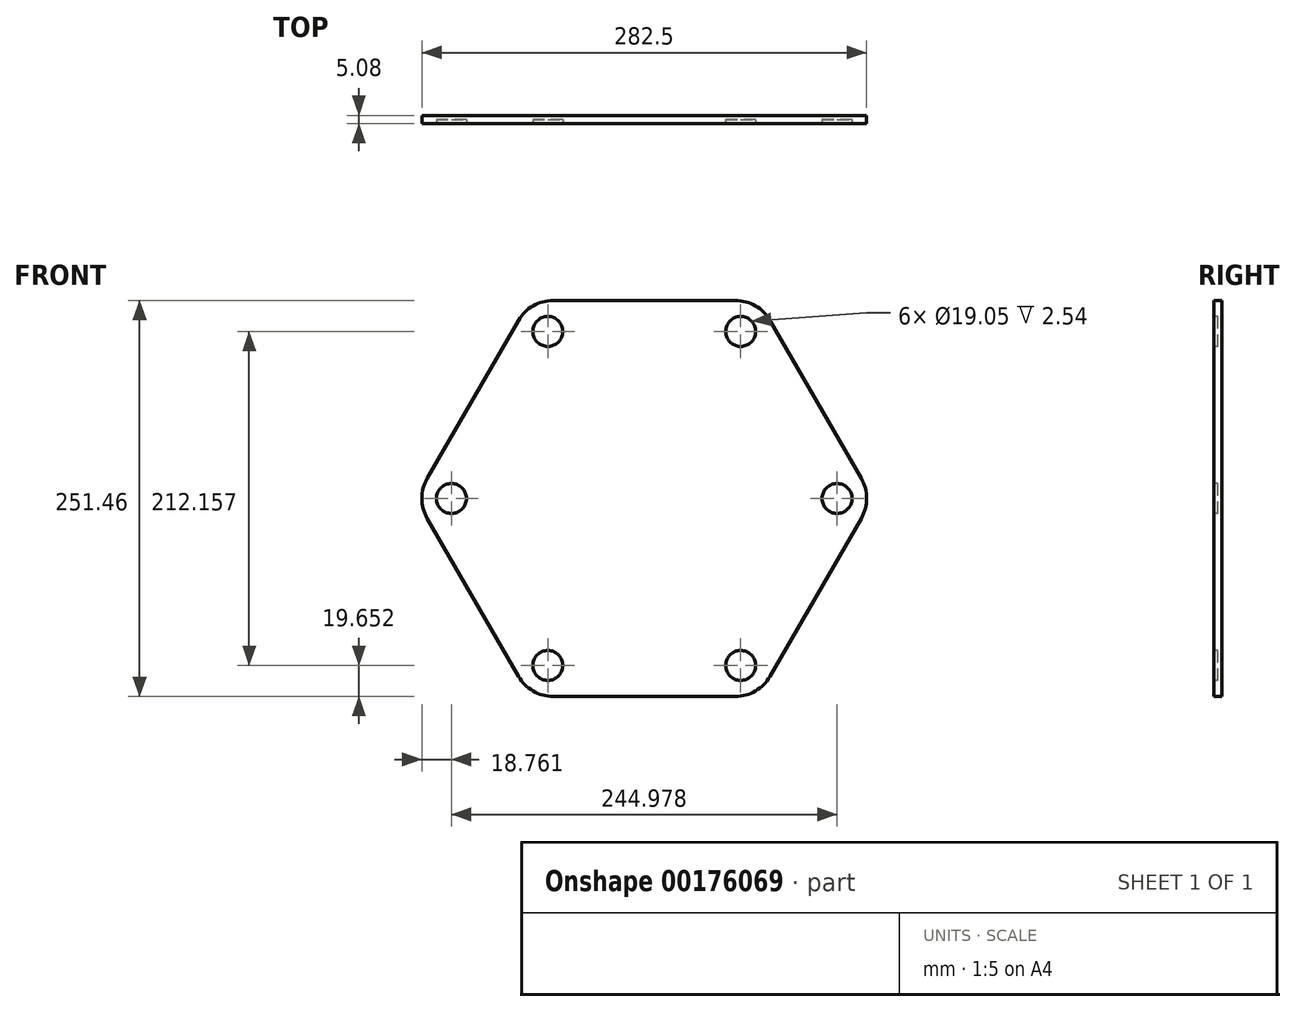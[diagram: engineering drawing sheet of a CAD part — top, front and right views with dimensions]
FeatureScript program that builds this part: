
annotation { "Feature Type Name" : "Feature", "Feature Type Description" : "" }
export const myFeature = defineFeature(function(context is Context, id is Id, definition is map)
    precondition{}
    {
        {
            var Q0;
            Q0=qCreatedBy(makeId("Front.planeOp"),FACE);
            var sketch = newSketch(context, id + "F0", { "sketchPlane" : qUnion([Q0])});
            skCircle(sketch, "E0.cCircle", {"center": v(0, 0) * mm, "radius": 125.73 * mm, "construction": true});
            skLineSegment(sketch, "E0.0", {"start": v(-57.93, 125.73) * mm, "end": v(57.93, 125.73) * mm});
            skLineSegment(sketch, "E0.1", {"start": v(79.92, 113.03) * mm, "end": v(137.85, 12.7) * mm});
            skLineSegment(sketch, "E0.2", {"start": v(137.85, -12.7) * mm, "end": v(79.92, -113.03) * mm});
            skLineSegment(sketch, "E0.3", {"start": v(57.93, -125.73) * mm, "end": v(-57.93, -125.73) * mm});
            skLineSegment(sketch, "E0.4", {"start": v(-79.92, -113.03) * mm, "end": v(-137.85, -12.7) * mm});
            skLineSegment(sketch, "E0.5", {"start": v(-137.85, 12.7) * mm, "end": v(-79.92, 113.03) * mm});
            skPoint(sketch, "E0.0.midPoint", {"position": v(0, 125.73) * mm});
            skPoint(sketch, "E1.visualSharp", {"position": v(-72.6, 125.73) * mm});
            skArc(sketch, "E1.filletArc", {"start": v(-57.93, 125.73) * mm, "mid": v(-70.63, 122.33) * mm, "end": v(-79.92, 113.03) * mm});
            skPoint(sketch, "E2.visualSharp", {"position": v(72.6, 125.73) * mm});
            skArc(sketch, "E2.filletArc", {"start": v(79.92, 113.03) * mm, "mid": v(70.63, 122.33) * mm, "end": v(57.93, 125.73) * mm});
            skPoint(sketch, "E3.visualSharp", {"position": v(145.18, 0) * mm});
            skArc(sketch, "E3.filletArc", {"start": v(137.85, -12.7) * mm, "mid": v(141.25, 0) * mm, "end": v(137.85, 12.7) * mm});
            skPoint(sketch, "E4.visualSharp", {"position": v(72.6, -125.73) * mm});
            skArc(sketch, "E4.filletArc", {"start": v(57.93, -125.73) * mm, "mid": v(70.63, -122.33) * mm, "end": v(79.92, -113.03) * mm});
            skPoint(sketch, "E5.visualSharp", {"position": v(-72.6, -125.73) * mm});
            skArc(sketch, "E5.filletArc", {"start": v(-79.92, -113.03) * mm, "mid": v(-70.63, -122.33) * mm, "end": v(-57.93, -125.73) * mm});
            skPoint(sketch, "E6.visualSharp", {"position": v(-145.18, 0) * mm});
            skArc(sketch, "E6.filletArc", {"start": v(-137.85, 12.7) * mm, "mid": v(-141.25, 0) * mm, "end": v(-137.85, -12.7) * mm});
            skSolve(sketch);
        }
        {
            var Q0;
            Q0=qSketchRegion(id+"F0",true);
            extrude(context, id + "F1", {"entities" : qUnion([Q0]), "depth" : 5.08 * mm});
        }
        {
            var Q0;
            Q0=makeQuery(id+"F1.opExtrude","CAP_FACE",FACE,{"disambiguationData":[OSD([sQuery(id+"F0.wireOp",EDGE,"89adff3a-a6a3-488e-98a2-3c8cfae46a67.0"),sQuery(id+"F0.wireOp",EDGE,"89adff3a-a6a3-488e-98a2-3c8cfae46a67.1"),sQuery(id+"F0.wireOp",EDGE,"89adff3a-a6a3-488e-98a2-3c8cfae46a67.2"),sQuery(id+"F0.wireOp",EDGE,"89adff3a-a6a3-488e-98a2-3c8cfae46a67.3"),sQuery(id+"F0.wireOp",EDGE,"89adff3a-a6a3-488e-98a2-3c8cfae46a67.4"),sQuery(id+"F0.wireOp",EDGE,"89adff3a-a6a3-488e-98a2-3c8cfae46a67.5"),sQuery(id+"F0.wireOp",EDGE,"E0.0"),sQuery(id+"F0.wireOp",EDGE,"E0.1"),sQuery(id+"F0.wireOp",EDGE,"E0.2"),sQuery(id+"F0.wireOp",EDGE,"E0.3"),sQuery(id+"F0.wireOp",EDGE,"E0.4"),sQuery(id+"F0.wireOp",EDGE,"E0.5"),sQuery(id+"F0.wireOp",EDGE,"E1.filletArc"),sQuery(id+"F0.wireOp",EDGE,"E2.filletArc"),sQuery(id+"F0.wireOp",EDGE,"E3.filletArc"),sQuery(id+"F0.wireOp",EDGE,"E4.filletArc"),sQuery(id+"F0.wireOp",EDGE,"E5.filletArc"),sQuery(id+"F0.wireOp",EDGE,"E6.filletArc"),sQuery(id+"F0.wireOp",EDGE,"f75249da-3de1-4f9c-be4c-0aa355bc9cf9.filletArc"),sQuery(id+"F0.wireOp",EDGE,"088ebd15-d55c-44c8-8f16-d2fa2b6b4741.filletArc"),sQuery(id+"F0.wireOp",EDGE,"63a53d0c-d41e-4784-a526-b75ee20c9be9.filletArc"),sQuery(id+"F0.wireOp",EDGE,"852531b2-fb37-4d6c-b13d-2e23ae91320b.filletArc"),sQuery(id+"F0.wireOp",EDGE,"de79ae46-3bb9-44d5-8b06-5674d42a0243.filletArc"),sQuery(id+"F0.wireOp",EDGE,"4720e62b-cf44-4874-a035-06e2f2aa46ec.filletArc")])],"isStart":false});
            var sketch = newSketch(context, id + "F2", { "sketchPlane" : qUnion([Q0])});
            skCircle(sketch, "E7", {"center": v(-61.24, 106.08) * mm, "radius": 9.53 * mm});
            skLineSegment(sketch, "E8", {"start": v(-72.6, 125.73) * mm, "end": v(-54.26, 93.98) * mm, "construction": true});
            skCircle(sketch, "E9.1.0", {"center": v(-122.49, 0) * mm, "radius": 9.53 * mm});
            skCircle(sketch, "E9.2.0", {"center": v(-61.24, -106.08) * mm, "radius": 9.53 * mm});
            skCircle(sketch, "E9.3.0", {"center": v(61.24, -106.08) * mm, "radius": 9.53 * mm});
            skCircle(sketch, "E9.4.0", {"center": v(122.49, 0) * mm, "radius": 9.53 * mm});
            skCircle(sketch, "E9.5.0", {"center": v(61.24, 106.08) * mm, "radius": 9.53 * mm});
            skPoint(sketch, "E9.center", {"position": v(0, 0) * mm});
            skCircle(sketch, "E10", {"center": v(0, 0) * mm, "radius": 108.52 * mm, "construction": true});
            skSolve(sketch);
        }
        {
            var Q0;
            Q0=qSketchRegion(id+"F2",true);
            var Q1;
            Q1=makeQuery(id+"F1.opExtrude","CAP_FACE",FACE,{"disambiguationData":[OSD([sQuery(id+"F0.wireOp",EDGE,"89adff3a-a6a3-488e-98a2-3c8cfae46a67.0"),sQuery(id+"F0.wireOp",EDGE,"89adff3a-a6a3-488e-98a2-3c8cfae46a67.1"),sQuery(id+"F0.wireOp",EDGE,"89adff3a-a6a3-488e-98a2-3c8cfae46a67.2"),sQuery(id+"F0.wireOp",EDGE,"89adff3a-a6a3-488e-98a2-3c8cfae46a67.3"),sQuery(id+"F0.wireOp",EDGE,"89adff3a-a6a3-488e-98a2-3c8cfae46a67.4"),sQuery(id+"F0.wireOp",EDGE,"89adff3a-a6a3-488e-98a2-3c8cfae46a67.5"),sQuery(id+"F0.wireOp",EDGE,"E0.0"),sQuery(id+"F0.wireOp",EDGE,"E0.1"),sQuery(id+"F0.wireOp",EDGE,"E0.2"),sQuery(id+"F0.wireOp",EDGE,"E0.3"),sQuery(id+"F0.wireOp",EDGE,"E0.4"),sQuery(id+"F0.wireOp",EDGE,"E0.5"),sQuery(id+"F0.wireOp",EDGE,"E1.filletArc"),sQuery(id+"F0.wireOp",EDGE,"E2.filletArc"),sQuery(id+"F0.wireOp",EDGE,"E3.filletArc"),sQuery(id+"F0.wireOp",EDGE,"E4.filletArc"),sQuery(id+"F0.wireOp",EDGE,"E5.filletArc"),sQuery(id+"F0.wireOp",EDGE,"E6.filletArc"),sQuery(id+"F0.wireOp",EDGE,"f75249da-3de1-4f9c-be4c-0aa355bc9cf9.filletArc"),sQuery(id+"F0.wireOp",EDGE,"088ebd15-d55c-44c8-8f16-d2fa2b6b4741.filletArc"),sQuery(id+"F0.wireOp",EDGE,"63a53d0c-d41e-4784-a526-b75ee20c9be9.filletArc"),sQuery(id+"F0.wireOp",EDGE,"852531b2-fb37-4d6c-b13d-2e23ae91320b.filletArc"),sQuery(id+"F0.wireOp",EDGE,"de79ae46-3bb9-44d5-8b06-5674d42a0243.filletArc"),sQuery(id+"F0.wireOp",EDGE,"4720e62b-cf44-4874-a035-06e2f2aa46ec.filletArc")])],"isStart":true});
            extrude(context, id + "F3", {"entities" : qUnion([Q0]), "operationType" : NewBodyOperationType.REMOVE, "oppositeDirection" : true, "endBoundEntityFace" : qUnion([Q1]), "depth" : 2.54 * mm});
        }
    });
